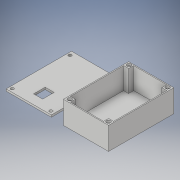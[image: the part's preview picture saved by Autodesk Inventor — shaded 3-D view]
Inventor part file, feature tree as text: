
AUTODESK INVENTOR PART (.ipt)
format: ipt  version: 2019 (Build 230136000, 136)  size: 162,816 bytes
history: native  units: mm
features: extrude x6, sketch x6, pattern_linear x3, shell x1
ambient origin geometry x8: Origin, YZ Plane, XZ Plane, XY Plane, X Axis, Y Axis, Z Axis, Center Point
bodies: Solid1 (feature_tree)
feature tree (16):
  extrude  "Extrusion1"  Depth=130.0mm
  shell  "Shell1"  Thickness=45.0mm
  extrude  "Extrusion2"  Depth=10.0mm
  pattern_linear  "Rectangular Pattern1"  Count1=2 Spacing1=116.0mm
  extrude  "Extrusion3"  Depth=76.0mm
  pattern_linear  "Rectangular Pattern2"  Count1=2 Spacing1=118.0mm
  extrude  "Extrusion4"  Depth=4.0mm
  extrude  "Extrusion5"  Depth=90.0mm
  pattern_linear  "Rectangular Pattern3"  Count1=13  [1 undecoded]
  extrude  "Extrusion6"  Depth=4.0mm TaperAngle=0.0deg
  sketch  "Sketch1"  dims[d0=90.0mm d1=130.0mm d2=45.0mm d3=0.0mm]
  sketch  "Sketch2"  dims[d4=2.0mm d5=10.0mm]
  sketch  "Sketch3"  dims[d6=10.0mm]
  sketch  "Sketch4"  dims[d7=43.0mm d8=0.0mm d9=20.0mm d11=116.0mm]
  sketch  "Sketch5"  dims[d12=20.0mm d14=76.0mm d15=8.0mm]
  sketch  "Sketch6"  dims[d16=4.0mm d17=0.0mm d18=20.0mm d20=118.0mm d21=20.0mm d23=77.0mm d24=90.0mm d25=130.0mm d26=4.0mm d27=0.0mm d28=4.0mm d29=0.0mm d30=20.0mm d32=115.0mm d33=20.0mm d35=77.0mm d36=9.0mm d37=23.0mm d38=18.0mm d39=4.0mm d40=0.0mm]
note: 1 required parameter value undecoded (feature->parameter linkage not recoverable at this tier; creation-order binding heuristic only, values carry confidence <= 0.55)
